# Revit family: Lighting_Outside_Focus-Lighting_Turn
name_source: partatom
category: Lighting Fixtures
revit_build: Autodesk Revit 2015 (Build: 20140903_1530(x64)
units: mm (PartAtom-declared; Revit-internal decimal feet)

## types (4) — shared parameters
BIMobject category = Outside
BIMobject category code = lighting-outside
BIMobject main category = Lighting
BIMobject main category code = lighting
BOSUseNativeGeometries = 1
Brand url = http://focus-lighting.dk
Color Filter = 16777215
Dimming Lamp Color Temperature Shift = <None>
Edition number = 1
IFC Classification = Lamp
Light Source Symbol Size = 2' - 0"
Manufacturer name = Focus Lighting
Masterformat 2014 Code = 12 43 13
Masterformat 2014 Description = Lamps
Material main = Aluminium
NBS Reference Code = 49
NBS Reference Description = Luminaires And Lamps
OmniClass Code = 23-35 45 15
OmniClass Description = Lamps
Product Guid = 5983fa09-cd81-4b54-80a8-bc5ff9d7ad9c
Product SKU = turn
Product certification = http://www.focus-lighting.dk
Product data url = https://bimobject.com
Product name = Turn
Product url = http://www.focus-lighting.dk
QR code = http://bimobject.com
Technical description = http://www.focus-lighting.dk
UNSPSC Code = 391016
Uniclass 1.4 Code = L7474
Uniclass 1.4 Description = Lamps
Uniclass 2.0 Code = PR-49
Uniclass 2.0 Description = Luminaires And Lamps
Uniclass 2015 Code = Pr_70_70_46
Uniclass 2015 Name = Lamps
zero-valued in all types: Nominal height, Nominal width, Weight Net (Kg)

## type names (no varying parameters)
- Default Colour - (Black RAL 9005)
- Default Colour - (Corten brown Mars 2525 YX355F)
- Default Colour - (Silver grey MW300D)
- Default Colour - (Graphite grey SW302G (close to RAL 9007))

## geometry (parser evidence)
native form markers: Sweep x1
no freeform markers — native parametric forms only
